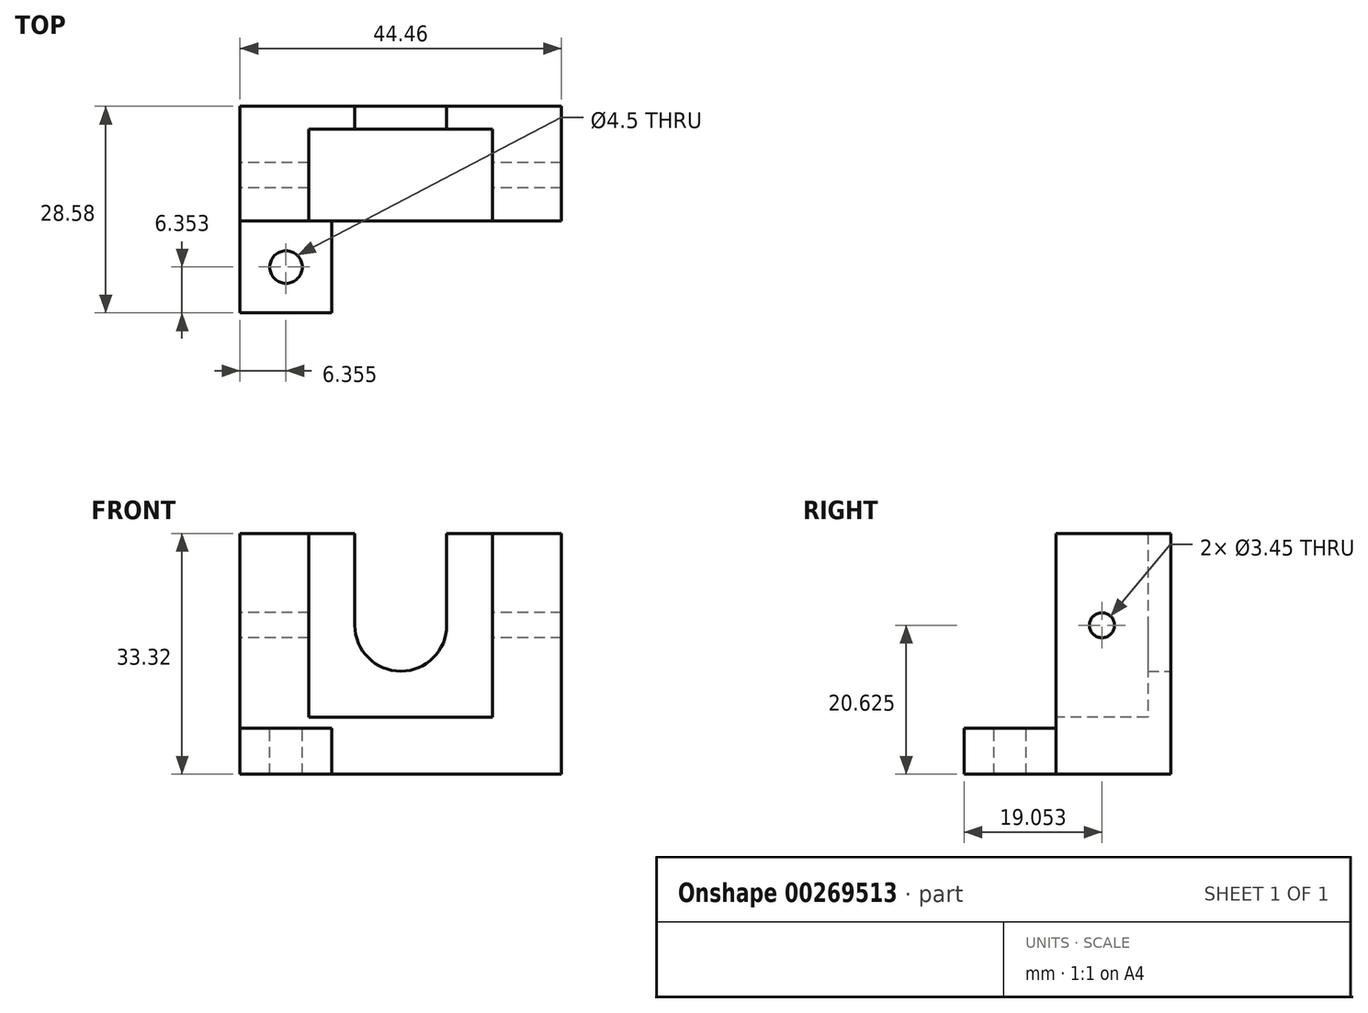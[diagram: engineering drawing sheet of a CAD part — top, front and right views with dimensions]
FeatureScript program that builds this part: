
annotation { "Feature Type Name" : "Feature", "Feature Type Description" : "" }
export const myFeature = defineFeature(function(context is Context, id is Id, definition is map)
    precondition{}
    {
        {
            var Q0;
            Q0=qCreatedBy(makeId("Front.planeOp"),FACE);
            var sketch = newSketch(context, id + "F0", { "sketchPlane" : qUnion([Q0])});
            skLineSegment(sketch, "E0.bottom", {"start": v(-22.23, 0) * mm, "end": v(22.23, 0) * mm});
            skLineSegment(sketch, "E0.top", {"start": v(-22.23, 33.32) * mm, "end": v(22.23, 33.32) * mm});
            skLineSegment(sketch, "E0.left", {"start": v(-22.23, 0) * mm, "end": v(-22.23, 33.32) * mm});
            skLineSegment(sketch, "E0.right", {"start": v(22.23, 0) * mm, "end": v(22.22, 33.32) * mm});
            skSolve(sketch);
        }
        {
            var Q0;
            Q0 = qSketchRegion(id + "F0", true);
            extrude(context, id + "F1", {"entities" : qUnion([Q0]), "endBound" : BoundingType.SYMMETRIC, "depth" : 15.88 * mm});
        }
        {
            var Q0;
            Q0=makeQuery(id+"F1.opExtrude","CAP_FACE",FACE,{"disambiguationData":[OSD([sQuery(id+"F0.wireOp",EDGE,"E0.bottom"),sQuery(id+"F0.wireOp",EDGE,"E0.top"),sQuery(id+"F0.wireOp",EDGE,"E0.left"),sQuery(id+"F0.wireOp",EDGE,"E0.right")])],"isStart":false});
            var sketch = newSketch(context, id + "F2", { "sketchPlane" : qUnion([Q0])});
            skLineSegment(sketch, "E1.bottom", {"start": v(-12.7, 33.32) * mm, "end": v(12.7, 33.32) * mm});
            skLineSegment(sketch, "E1.top", {"start": v(-12.7, 7.92) * mm, "end": v(12.7, 7.92) * mm});
            skLineSegment(sketch, "E1.left", {"start": v(-12.7, 33.32) * mm, "end": v(-12.7, 7.92) * mm});
            skLineSegment(sketch, "E1.right", {"start": v(12.7, 33.32) * mm, "end": v(12.7, 7.92) * mm});
            skSolve(sketch);
        }
        {
            var Q0;
            Q0 = qSketchRegion(id + "F2", true);
            extrude(context, id + "F3", {"entities" : qUnion([Q0]), "operationType" : NewBodyOperationType.REMOVE, "oppositeDirection" : true, "depth" : 12.7 * mm});
        }
        {
            var Q0;
            Q0=makeQuery(id+"F1.opExtrude","CAP_FACE",FACE,{"disambiguationData":[OSD([sQuery(id+"F0.wireOp",EDGE,"E0.bottom"),sQuery(id+"F0.wireOp",EDGE,"E0.top"),sQuery(id+"F0.wireOp",EDGE,"E0.left"),sQuery(id+"F0.wireOp",EDGE,"E0.right")])],"isStart":false});
            var sketch = newSketch(context, id + "F4", { "sketchPlane" : qUnion([Q0])});
            skPoint(sketch, "E2", {"position": v(-12.7, 7.92) * mm});
            skPoint(sketch, "E3", {"position": v(12.7, 7.92) * mm});
            skSolve(sketch);
        }
        {
            var Q0;
            Q0=makeQuery(id+"F3.boolean.opBoolean","COPY",FACE,{"derivedFrom":makeQuery(id+"F3.opExtrude","CAP_FACE",FACE,{"disambiguationData":[OSD([sQuery(id+"F2.wireOp",EDGE,"E1.bottom"),sQuery(id+"F2.wireOp",EDGE,"E1.top"),sQuery(id+"F2.wireOp",EDGE,"E1.left"),sQuery(id+"F2.wireOp",EDGE,"E1.right")])],"isStart":false})});
            var sketch = newSketch(context, id + "F5", { "sketchPlane" : qUnion([Q0])});
            skLineSegment(sketch, "E4.bottom", {"start": v(-6.35, 33.32) * mm, "end": v(6.35, 33.32) * mm});
            skLineSegment(sketch, "E4.top", {"start": v(-6.35, 14.27) * mm, "end": v(6.35, 14.27) * mm});
            skLineSegment(sketch, "E4.left", {"start": v(6.35, 33.32) * mm, "end": v(6.35, 14.27) * mm});
            skLineSegment(sketch, "E4.right", {"start": v(-6.35, 33.32) * mm, "end": v(-6.35, 14.27) * mm});
            skSolve(sketch);
        }
        {
            var Q0;
            Q0 = qSketchRegion(id + "F5", true);
            extrude(context, id + "F6", {"entities" : qUnion([Q0]), "operationType" : NewBodyOperationType.REMOVE, "endBound" : BoundingType.THROUGH_ALL, "oppositeDirection" : true, "depth" : 25.4 * mm});
        }
        {
            var Q0;
            Q0=makeQuery(id+"F6.boolean.opBoolean","COPY",EDGE,{"derivedFrom":makeQuery(id+"F6.opExtrude","SWEPT_EDGE",EDGE,{"disambiguationData":[OSD([sQuery(id+"F5.wireOp",EDGE,"E4.top"),sQuery(id+"F5.wireOp",EDGE,"E4.right")])]})});
            var Q1;
            Q1=makeQuery(id+"F6.boolean.opBoolean","COPY",EDGE,{"derivedFrom":makeQuery(id+"F6.opExtrude","SWEPT_EDGE",EDGE,{"disambiguationData":[OSD([sQuery(id+"F5.wireOp",EDGE,"E4.top"),sQuery(id+"F5.wireOp",EDGE,"E4.left")])]})});
            fillet(context, id + "F7", {"entities" : qUnion([Q0, Q1]), "radius" : 6.35 * mm, "tangentPropagation" : true, "allowEdgeOverflow" : false});
        }
        {
            var Q0;
            Q0=makeQuery(id+"F1.opExtrude","SWEPT_FACE",FACE,{"disambiguationData":[OSD([sQuery(id+"F0.wireOp",EDGE,"E0.left")])]});
            var sketch = newSketch(context, id + "F8", { "sketchPlane" : qUnion([Q0])});
            skLineSegment(sketch, "E5.bottom", {"start": v(20.64, 0) * mm, "end": v(7.94, 0) * mm});
            skLineSegment(sketch, "E5.top", {"start": v(20.64, 6.35) * mm, "end": v(7.94, 6.35) * mm});
            skLineSegment(sketch, "E5.left", {"start": v(20.64, 0) * mm, "end": v(20.64, 6.35) * mm});
            skLineSegment(sketch, "E5.right", {"start": v(7.94, 0) * mm, "end": v(7.94, 6.35) * mm});
            skSolve(sketch);
        }
        {
            var Q0;
            Q0=makeQuery(id+"F8.imprint","IMPRINT",FACE,{"disambiguationData":[TD([[makeQuery(id+"F8.imprint","IMPRINT",EDGE,{"derivedFrom":sQuery(id+"F8.wireOp",EDGE,"E5.bottom")}),-1.0]])]});
            var Q1;
            Q1=makeQuery(id+"F1.opExtrude","CAP_FACE",FACE,{"disambiguationData":[OSD([sQuery(id+"F0.wireOp",EDGE,"E0.bottom"),sQuery(id+"F0.wireOp",EDGE,"E0.top"),sQuery(id+"F0.wireOp",EDGE,"E0.left"),sQuery(id+"F0.wireOp",EDGE,"E0.right")])],"isStart":true});
            extrude(context, id + "F9", {"entities" : qUnion([Q0]), "operationType" : NewBodyOperationType.ADD, "oppositeDirection" : true, "endBoundEntityFace" : qUnion([Q1]), "depth" : 12.7 * mm});
        }
        {
            var Q0;
            Q0=makeQuery(id+"F9.opExtrude","SWEPT_FACE",FACE,{"disambiguationData":[OSD([sQuery(id+"F8.wireOp",EDGE,"E5.top")])]});
            var sketch = newSketch(context, id + "F10", { "sketchPlane" : qUnion([Q0])});
            skPoint(sketch, "E6", {"position": v(-15.87, -14.29) * mm});
            skPoint(sketch, "E6.positionSnap0", {"position": v(-15.87, -20.64) * mm});
            skPoint(sketch, "E6.positionSnap1", {"position": v(-9.53, -14.29) * mm});
            skSolve(sketch);
        }
        {
            var Q0;
            Q0=sQuery(id+"F10.wireOp",VERTEX,"E6");
            var Q1;
            Q1=makeQuery(id+"F1.opExtrude","SWEPT_BODY",BODY,{"disambiguationData":[OSD([sQuery(id+"F0.wireOp",EDGE,"E0.bottom"),sQuery(id+"F0.wireOp",EDGE,"E0.top"),sQuery(id+"F0.wireOp",EDGE,"E0.left"),sQuery(id+"F0.wireOp",EDGE,"E0.right")])]});
            hole(context, id + "F11", {"style" : HoleStyle.SIMPLE, "endStyle" : HoleEndStyle.THROUGH, "standardTappedOrClearance" : lookupTablePath({ "standard" : "ANSI", "fit" : "Normal (ASME)", "size" : "#8", "type" : "Clearance" }), "standardBlindInLast" : lookupTablePath({ "fit" : "Free", "standard" : "ANSI", "size" : "#8", "type" : "Clearance" }), "holeDiameter" : 4.5 * mm, "tappedDepth" : 9.52 * mm, "tapClearance" : 3, "locations" : qUnion([Q0]), "scope" : qUnion([Q1])});
        }
        {
            var Q0;
            Q0=makeQuery(id+"F1.opExtrude","SWEPT_FACE",FACE,{"disambiguationData":[OSD([sQuery(id+"F0.wireOp",EDGE,"E0.left")])]});
            var sketch = newSketch(context, id + "F12", { "sketchPlane" : qUnion([Q0])});
            skLineSegment(sketch, "E7.0", {"start": v(-4.76, 33.32) * mm, "end": v(-4.76, 7.92) * mm, "construction": true});
            skLineSegment(sketch, "E8", {"start": v(-4.76, 20.62) * mm, "end": v(7.94, 20.62) * mm, "construction": true});
            skPoint(sketch, "E9", {"position": v(1.59, 20.62) * mm});
            skLineSegment(sketch, "E10.0", {"start": v(-4.76, 7.92) * mm, "end": v(7.94, 7.92) * mm});
            skSolve(sketch);
        }
        {
            var Q0;
            Q0=sQuery(id+"F12.wireOp",VERTEX,"E9");
            var Q1;
            Q1=makeQuery(id+"F1.opExtrude","SWEPT_BODY",BODY,{"disambiguationData":[OSD([sQuery(id+"F0.wireOp",EDGE,"E0.bottom"),sQuery(id+"F0.wireOp",EDGE,"E0.top"),sQuery(id+"F0.wireOp",EDGE,"E0.left"),sQuery(id+"F0.wireOp",EDGE,"E0.right")])]});
            hole(context, id + "F13", {"style" : HoleStyle.SIMPLE, "endStyle" : HoleEndStyle.THROUGH, "standardTappedOrClearance" : lookupTablePath({ "standard" : "ANSI", "engagement" : "75%", "pitch" : "32 tpi", "size" : "#8", "type" : "Tapped" }), "standardBlindInLast" : lookupTablePath({ "standard" : "ANSI", "engagement" : "75%", "pitch" : "32 tpi", "size" : "#8", "type" : "Tapped" }), "holeDiameter" : 3.45 * mm, "showTappedDepth" : true, "tappedDepth" : 10.16 * mm, "tapClearance" : 3, "locations" : qUnion([Q0]), "scope" : qUnion([Q1]), "majorDiameter" : 4.17 * mm});
        }
        {
            var Q0;
            {var subQ0=sQuery(id+"F8.wireOp",EDGE,"E5.bottom");Q0=makeQuery(id+"FieTtfTv61oYAmp_1.1.F9.boolean.opBoolean","MERGE",FACE,{"derivedFrom":[makeQuery(id+"F9.boolean.opBoolean","MERGE",FACE,{"derivedFrom":[makeQuery(id+"F1.opExtrude","SWEPT_FACE",FACE,{"disambiguationData":[OSD([sQuery(id+"F0.wireOp",EDGE,"E0.bottom")])]}),makeQuery(id+"F9.opExtrude","SWEPT_FACE",FACE,{"disambiguationData":[OSD([subQ0])]})]}),makeQuery(id+"FieTtfTv61oYAmp_1.1.F9.opExtrude","SWEPT_FACE",FACE,{"disambiguationData":[OSD([subQ0])]})]});}
            var sketch = newSketch(context, id + "F14", { "sketchPlane" : qUnion([Q0])});
            skSolve(sketch);
        }
    });
